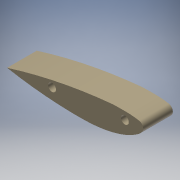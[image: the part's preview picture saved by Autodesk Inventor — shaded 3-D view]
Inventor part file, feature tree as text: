
AUTODESK INVENTOR PART (.ipt)
format: ipt  version: 2018 (Build 220112000, 112)  size: 121,344 bytes
history: native  units: mm
features: extrude x1, sketch x1, projected_geometry x1
ambient origin geometry x8: Origin, YZ Plane, XZ Plane, XY Plane, X Axis, Y Axis, Z Axis, Center Point
bodies: Body1 (feature_tree)
feature tree (3):
  extrude  "押し出し2"  Depth=44.75mm TaperAngle=0.0deg
  sketch  "スケッチ1"
  projected_geometry  "投影ループ1"
